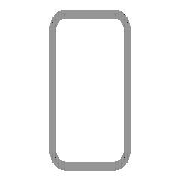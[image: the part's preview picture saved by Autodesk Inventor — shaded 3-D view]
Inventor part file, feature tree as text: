
AUTODESK INVENTOR PART (.ipt)
format: ipt  version: 2025 (Build 290162010, 162A)  size: 134,144 bytes
history: native  units: mm (DEFAULTED — no unit token found)
features: other x4, sketch x1, plane x1
ambient origin geometry x8: Origin, YZ Plane, XZ Plane, XY Plane, X Axis, Y Axis, Z Axis, Center Point
bodies: Solid1 (feature_tree), Body (feature_tree)
feature tree (6):
  parser-record x1  (decoder bookkeeping rows leaked as tree rows — omitted from the tree; the rows remain in map.json)
  other  "Driven Length"
  other  "Start Plane"
  other  "End Plane"
  sketch  "Sketch3"  dims[d3=1170.0mm d4=0.0mm d7=4.0mm d9=40.0mm d11=80.0mm d12=2.0mm d13=40.0mm d14=1210.0mm d15=20.0mm d16=40.0mm d17=90.0deg d18=1170.0mm]
  plane  "Work Plane3"
